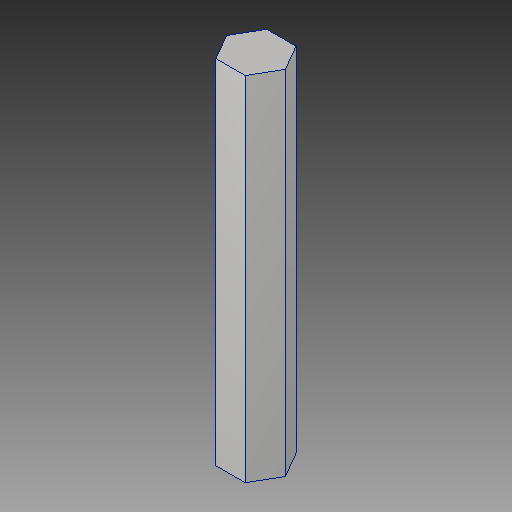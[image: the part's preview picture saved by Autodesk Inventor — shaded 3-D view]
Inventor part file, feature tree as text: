
AUTODESK INVENTOR PART (.ipt)
format: ipt  version: 2018 (Build 220112000, 112)  size: 95,744 bytes
history: native  units: in
note: dims shown in document units (in); Inventor stores cm internally (conversion verified against a paired STEP export)
features: extrude x1, sketch x1
ambient origin geometry x8: Origin, YZ Plane, XZ Plane, XY Plane, X Axis, Y Axis, Z Axis, Center Point
bodies: Solid1 (feature_tree)
feature tree (2):
  extrude  "Extrusion1"  Depth=3.5in TaperAngle=0.0deg
  sketch  "Sketch1"  dims[d0=0.582in d1=3.5in d2=0.0in]
